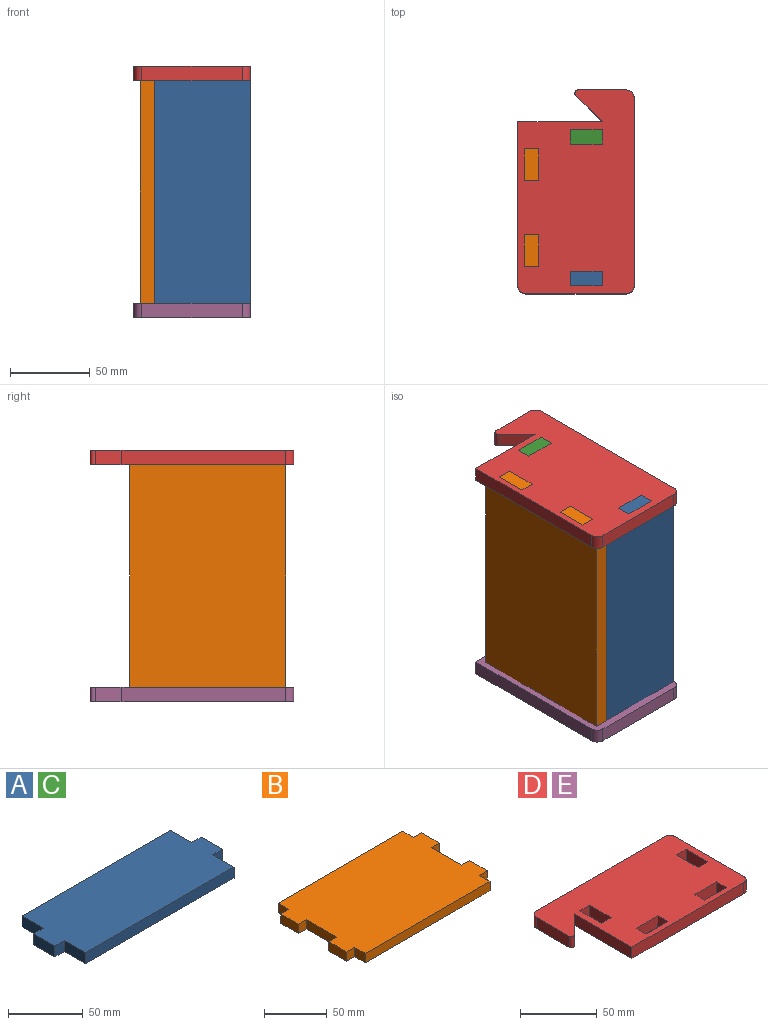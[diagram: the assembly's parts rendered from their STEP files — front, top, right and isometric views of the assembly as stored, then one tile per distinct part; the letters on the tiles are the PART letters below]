
ASSEMBLY  parts=5 mates=4
PART A: 14 faces, bbox 158x60x9 mm
  f0: plane 140x9mm, normal (0,1,0), area 1260mm2, adj f1,f11,f12,f13
  f1: plane 20x9mm, normal (-1,0,0), area 180mm2, adj f0,f2,f12,f13
  f2: plane 9x9mm, normal (0,1,0), area 81mm2, adj f1,f3,f12,f13
  f3: plane 20x9mm, normal (-1,0,0), area 180mm2, adj f2,f4,f12,f13
  f4: plane 9x9mm, normal (0,-1,0), area 81mm2, adj f3,f5,f12,f13
  f5: plane 20x9mm, normal (-1,0,0), area 180mm2, adj f4,f6,f12,f13
  f6: plane 140x9mm, normal (0,-1,0), area 1260mm2, adj f5,f7,f12,f13
  f7: plane 20x9mm, normal (1,0,0), area 180mm2, adj f6,f8,f12,f13
  f8: plane 9x9mm, normal (0,-1,0), area 81mm2, adj f7,f9,f12,f13
  f9: plane 20x9mm, normal (1,0,0), area 180mm2, adj f8,f10,f12,f13
  f10: plane 9x9mm, normal (0,1,0), area 81mm2, adj f9,f11,f12,f13
  f11: plane 20x9mm, normal (1,0,0), area 180mm2, adj f0,f10,f12,f13
  f12: plane 158x60mm, normal (0,0,1), area 8760mm2, adj f0,f1,f2,f3,f4,f5,f6,f7
  f13: plane 158x60mm, normal (0,0,-1), area 8760mm2, adj f0,f1,f2,f3,f4,f5,f6,f7
PART B: 22 faces, bbox 158x98x9 mm
  f0: plane 140x9mm, normal (0,1,0), area 1260mm2, adj f1,f19,f20,f21
  f1: plane 12x9mm, normal (-1,0,0), area 108mm2, adj f0,f2,f20,f21
  f2: plane 9x9mm, normal (0,1,0), area 81mm2, adj f1,f3,f20,f21
  f3: plane 20x9mm, normal (-1,0,0), area 180mm2, adj f2,f4,f20,f21
  f4: plane 9x9mm, normal (0,-1,0), area 81mm2, adj f3,f5,f20,f21
  f5: plane 34x9mm, normal (-1,0,0), area 306mm2, adj f4,f6,f20,f21
  f6: plane 9x9mm, normal (0,1,0), area 81mm2, adj f5,f7,f20,f21
  f7: plane 20x9mm, normal (-1,0,0), area 180mm2, adj f6,f8,f20,f21
  f8: plane 9x9mm, normal (0,-1,0), area 81mm2, adj f7,f9,f20,f21
  f9: plane 12x9mm, normal (-1,0,0), area 108mm2, adj f8,f10,f20,f21
  f10: plane 140x9mm, normal (0,-1,0), area 1260mm2, adj f9,f11,f20,f21
  f11: plane 12x9mm, normal (1,0,0), area 108mm2, adj f10,f12,f20,f21
  f12: plane 9x9mm, normal (0,-1,0), area 81mm2, adj f11,f13,f20,f21
  f13: plane 20x9mm, normal (1,0,0), area 180mm2, adj f12,f14,f20,f21
  f14: plane 9x9mm, normal (0,1,0), area 81mm2, adj f13,f15,f20,f21
  f15: plane 34x9mm, normal (1,0,0), area 306mm2, adj f14,f16,f20,f21
  f16: plane 9x9mm, normal (0,-1,0), area 81mm2, adj f15,f17,f20,f21
  f17: plane 20x9mm, normal (1,0,0), area 180mm2, adj f16,f18,f20,f21
  f18: plane 9x9mm, normal (0,1,0), area 81mm2, adj f17,f19,f20,f21
  f19: plane 12x9mm, normal (1,0,0), area 108mm2, adj f0,f18,f20,f21
  f20: plane 158x98mm, normal (0,0,1), area 14440mm2, adj f0,f1,f2,f3,f4,f5,f6,f7
  f21: plane 158x98mm, normal (0,0,-1), area 14440mm2, adj f0,f1,f2,f3,f4,f5,f6,f7
PART C: same geometry as A
PART D: 28 faces, bbox 128x73x9 mm
  f0: plane 20x9mm, normal (0,1,0), area 180mm2, adj f1,f21,f22,f23
  f1: plane 9x9mm, normal (1,0,0), area 81mm2, adj f0,f2,f22,f23
  f2: plane 20x9mm, normal (0,-1,0), area 180mm2, adj f1,f21,f22,f23
  f3: plane 20x9mm, normal (0,1,0), area 180mm2, adj f4,f17,f22,f23
  f4: plane 9x9mm, normal (1,0,0), area 81mm2, adj f3,f5,f22,f23
  f5: plane 20x9mm, normal (0,-1,0), area 180mm2, adj f4,f17,f22,f23
  f6: plane 20x9mm, normal (1,0,0), area 180mm2, adj f7,f18,f22,f23
  f7: plane 9x9mm, normal (0,-1,0), area 81mm2, adj f6,f8,f22,f23
  f8: plane 20x9mm, normal (-1,0,0), area 180mm2, adj f7,f18,f22,f23
  f9: plane 20x9mm, normal (1,0,0), area 180mm2, adj f10,f19,f22,f23
  f10: plane 9x9mm, normal (0,-1,0), area 81mm2, adj f9,f11,f22,f23
  f11: plane 20x9mm, normal (-1,0,0), area 180mm2, adj f10,f19,f22,f23
  f12: plane 30.17x9mm, normal (-1,0,0), area 271.5mm2, adj f22,f23,f24,f27
  f13: plane 16.59x16.59mm, normal (0.71,-0.71,0), area 211.1mm2, adj f14,f22,f23,f24
  f14: plane 53x9mm, normal (-1,0,0), area 477mm2, adj f13,f15,f22,f23
  f15: plane 103x9mm, normal (0,-1,0), area 927mm2, adj f14,f22,f23,f25
  f16: plane 63x9mm, normal (1,0,0), area 567mm2, adj f22,f23,f25,f26
  f17: plane 9x9mm, normal (-1,0,0), area 81mm2, adj f3,f5,f22,f23
  f18: plane 9x9mm, normal (0,1,0), area 81mm2, adj f6,f8,f22,f23
  f19: plane 9x9mm, normal (0,1,0), area 81mm2, adj f9,f11,f22,f23
  f20: plane 118x9mm, normal (0,1,0), area 1062mm2, adj f22,f23,f26,f27
  f21: plane 9x9mm, normal (-1,0,0), area 81mm2, adj f0,f2,f22,f23
  f22: plane 128x73mm, normal (0,0,1), area 7743mm2, adj f0,f1,f2,f3,f4,f5,f6,f7
  f23: plane 128x73mm, normal (0,0,-1), area 7743mm2, adj f0,f1,f2,f3,f4,f5,f6,f7
  f24: cylinder r=2mm len=9mm, axis (0,0,1), area 42.4mm2, adj f12,f13,f22,f23
  f25: cylinder r=5mm len=9mm, axis (0,0,1), area 70.7mm2, adj f15,f16,f22,f23
  f26: cylinder r=5mm len=9mm, axis (0,0,-1), area 70.7mm2, adj f16,f20,f22,f23
  f27: cylinder r=5mm len=9mm, axis (0,0,-1), area 70.7mm2, adj f12,f20,f22,f23
PART E: same geometry as D
PLACE A rot(axis=(0.58,0.58,-0.58),120deg) t=(127.43,62.71,-77.16)mm
PLACE B rot(axis=(0.71,0,0.71),180deg) t=(88.43,102.71,-77.16)mm
PLACE C rot(axis=(-0.58,0.58,0.58),120deg) t=(127.43,142.71,-77.16)mm
PLACE D rot(axis=(0,0,-1),90deg) t=(137.43,156.71,-7.16)mm
PLACE E rot(axis=(0,0,-1),90deg) t=(137.43,156.71,-156.16)mm
MATE fastened D.f22 <-> B.f13  axis (0,0,1) through (92.93,129.71,1.84)mm
MATE fastened C.f3 <-> D.f22  axis (0,0,1) through (127.43,147.21,1.84)mm
MATE fastened E.f23 <-> B.f7  axis (0,0,-1) through (92.93,129.71,-156.16)mm
MATE fastened A.f9 <-> E.f23  axis (0,0,-1) through (127.43,58.21,-156.16)mm
